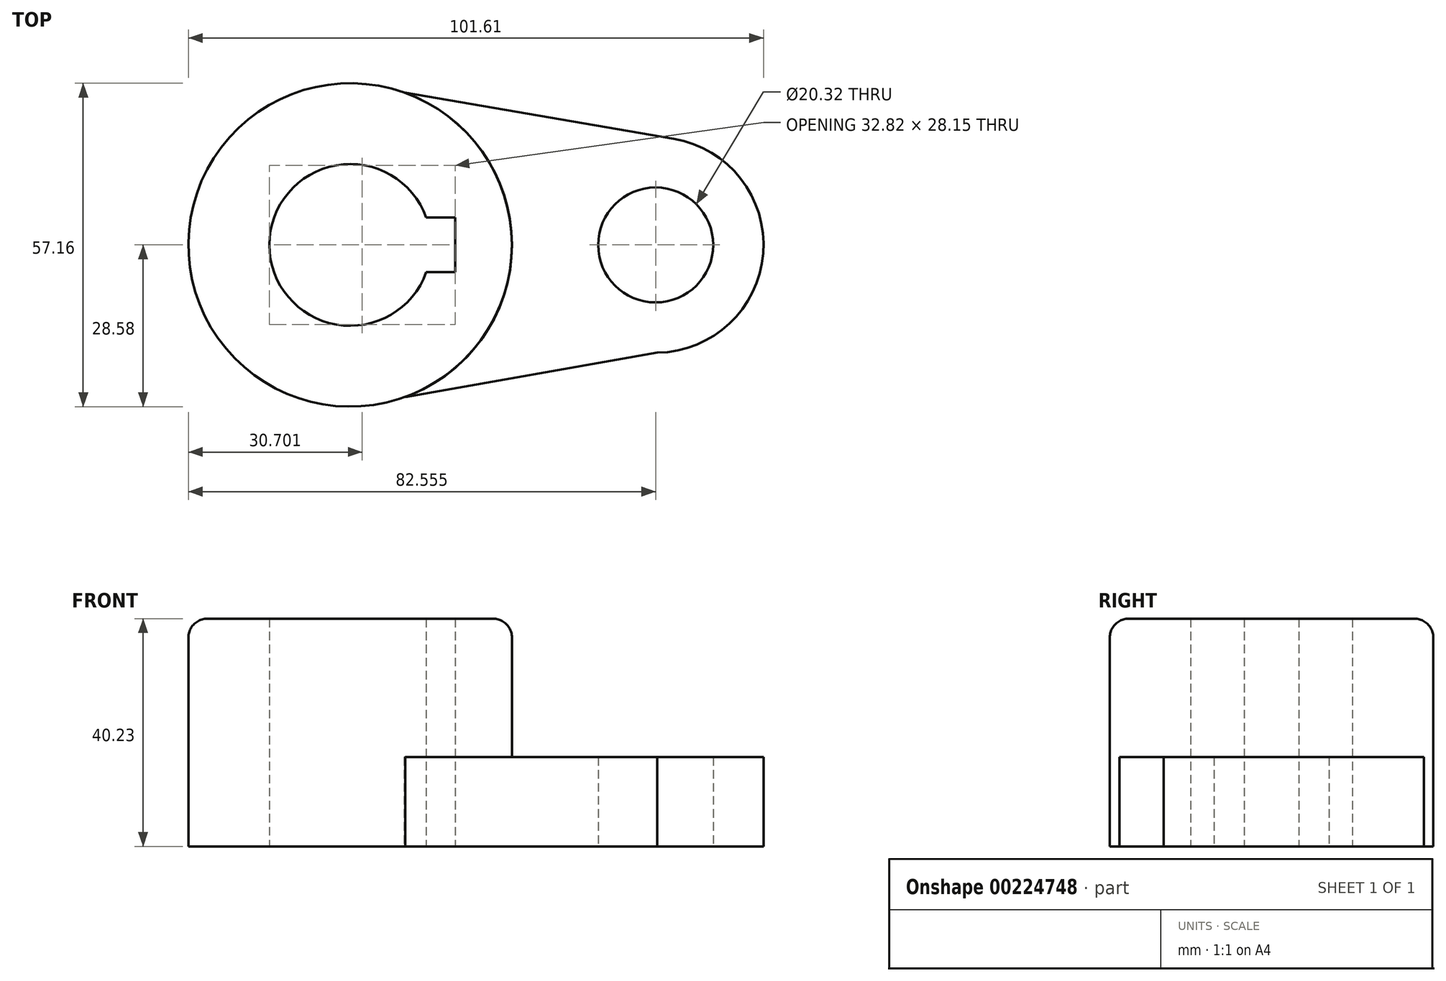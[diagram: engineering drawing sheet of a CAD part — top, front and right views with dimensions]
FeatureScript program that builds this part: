
annotation { "Feature Type Name" : "Feature", "Feature Type Description" : "" }
export const myFeature = defineFeature(function(context is Context, id is Id, definition is map)
    precondition{}
    {
        {
            var Q0;
            Q0=qCreatedBy(makeId("Top.planeOp"),FACE);
            var sketch = newSketch(context, id + "F0", { "sketchPlane" : qUnion([Q0])});
            skCircle(sketch, "E0", {"center": v(0, 0) * mm, "radius": 28.58 * mm});
            skArc(sketch, "E1", {"start": v(13.45, 4.83) * mm, "mid": v(-14.29, 0) * mm, "end": v(13.45, -4.83) * mm});
            skLineSegment(sketch, "E2.bottom", {"start": v(18.53, -4.83) * mm, "end": v(13.45, -4.83) * mm});
            skLineSegment(sketch, "E2.top", {"start": v(18.53, 4.83) * mm, "end": v(13.45, 4.83) * mm});
            skLineSegment(sketch, "E2.left", {"start": v(18.53, -4.83) * mm, "end": v(18.53, 4.83) * mm});
            skPoint(sketch, "E2.right.end.orphan", {"position": v(-18.53, 4.83) * mm});
            skPoint(sketch, "E3.orphan", {"position": v(-18.53, -4.83) * mm});
            skPoint(sketch, "E4.start.orphan", {"position": v(-14.29, 0) * mm});
            skLineSegment(sketch, "E5", {"start": v(0, 0) * mm, "end": v(53.98, 0) * mm});
            skCircle(sketch, "E6", {"center": v(53.98, 0) * mm, "radius": 10.16 * mm});
            skArc(sketch, "E7", {"start": v(54.23, -19.05) * mm, "mid": v(72.97, -1.48) * mm, "end": v(57.2, 18.78) * mm});
            skLineSegment(sketch, "E8", {"start": v(9.51, 26.95) * mm, "end": v(57.2, 18.78) * mm});
            skLineSegment(sketch, "E9", {"start": v(9.74, -26.86) * mm, "end": v(54.23, -19.05) * mm});
            skPoint(sketch, "E10.orphan", {"position": v(0, 28.58) * mm});
            skPoint(sketch, "E11.orphan", {"position": v(0, -28.58) * mm});
            skSolve(sketch);
        }
        {
            var Q0;
            Q0=makeQuery(id+"F0.imprint","IMPRINT",FACE,{"disambiguationData":[TD([[makeQuery(id+"F0.imprint","IMPRINT",EDGE,{"derivedFrom":sQuery(id+"F0.wireOp",EDGE,"E0")}),1.0]])]});
            extrude(context, id + "F1", {"entities" : qUnion([Q0]), "depth" : 40.23 * mm});
        }
        {
            var Q0;
            Q0=makeQuery(id+"F0.imprint","IMPRINT",FACE,{"disambiguationData":[TD([[makeQuery(id+"F0.imprint","IMPRINT",EDGE,{"derivedFrom":sQuery(id+"F0.wireOp",EDGE,"E6")}),-1.0]])]});
            extrude(context, id + "F2", {"entities" : qUnion([Q0]), "operationType" : NewBodyOperationType.ADD, "depth" : 15.77 * mm});
        }
        {
            var Q0;
            {var subQ0=sQuery(id+"F0.wireOp",EDGE,"E0");Q0=makeQuery(id+"F1.opExtrude","CAP_EDGE",EDGE,{"disambiguationData":[OSD([subQ0]),TDD([makeQuery(id+"F0.imprint","IMPRINT",EDGE,{"disambiguationData":[TD([[makeQuery(id+"F0.imprint","INTERSECT",VERTEX,{"disambiguationData":[OD(0.0)],"derivedFrom":[subQ0,sQuery(id+"F0.wireOp",EDGE,"E8")]}),-1.0]])],"derivedFrom":subQ0})])],"isStart":false});}
            fillet(context, id + "F3", {"entities" : qUnion([Q0]), "radius" : 3.3 * mm, "tangentPropagation" : true, "allowEdgeOverflow" : false});
        }
    });
